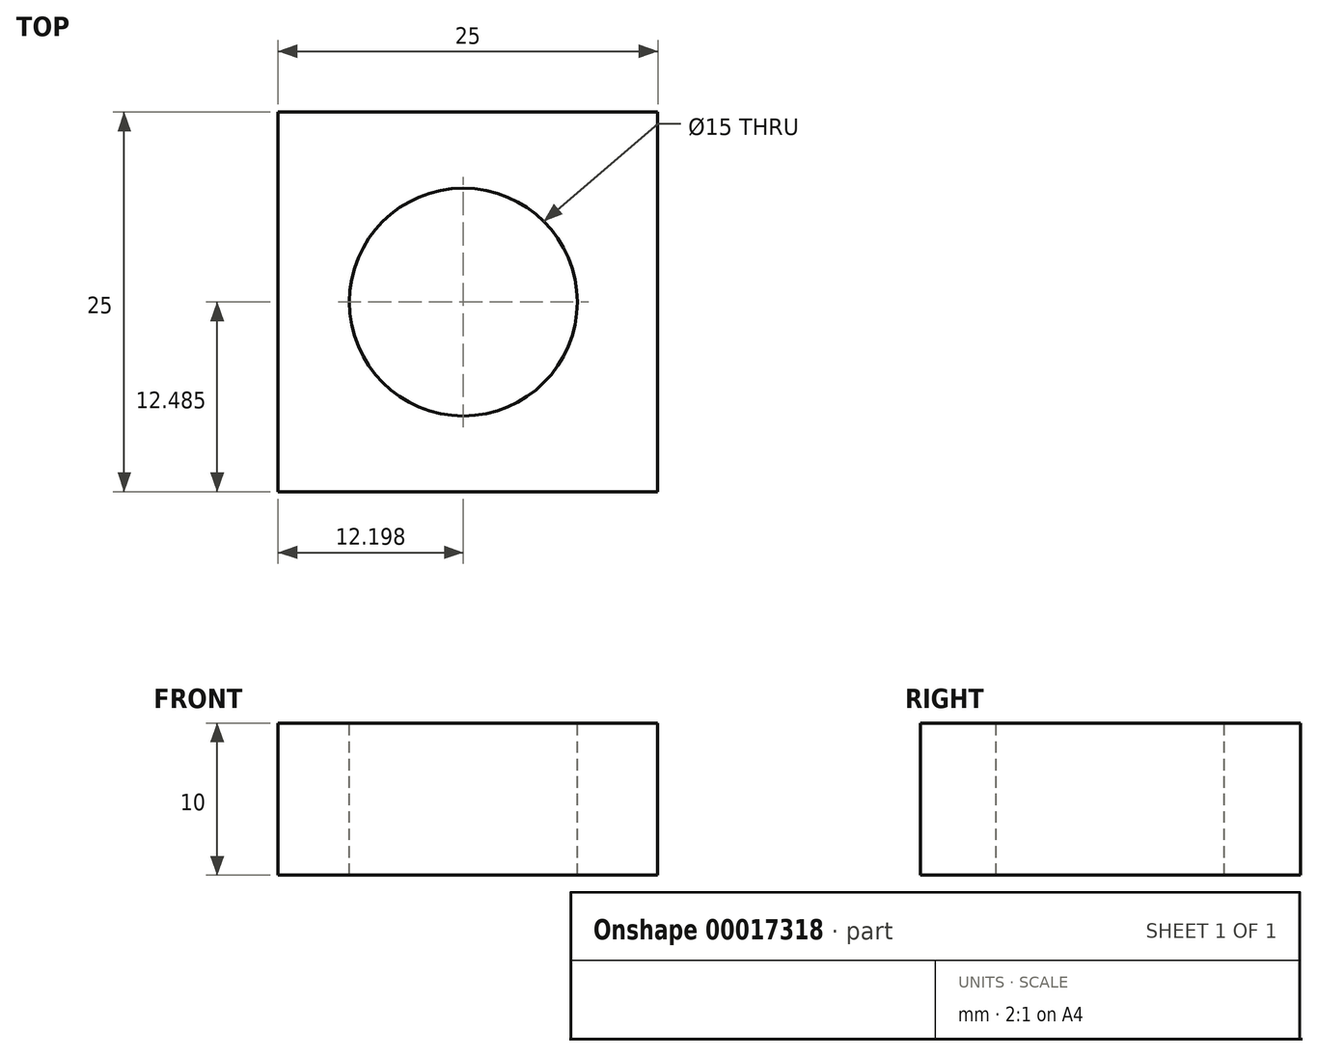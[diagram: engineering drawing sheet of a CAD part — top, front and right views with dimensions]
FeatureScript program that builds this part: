
annotation { "Feature Type Name" : "Feature", "Feature Type Description" : "" }
export const myFeature = defineFeature(function(context is Context, id is Id, definition is map)
    precondition{}
    {
        {
            var Q0;
            Q0=qCreatedBy(makeId("Front.planeOp"),FACE);
            var sketch = newSketch(context, id + "F0", { "sketchPlane" : qUnion([Q0])});
            skLineSegment(sketch, "E0", {"start": v(-4.12, 15.62) * mm, "end": v(-4.12, 5.62) * mm});
            skLineSegment(sketch, "E1", {"start": v(-4.12, 15.62) * mm, "end": v(20.88, 15.62) * mm});
            skLineSegment(sketch, "E2", {"start": v(20.88, 15.62) * mm, "end": v(20.88, 5.62) * mm});
            skLineSegment(sketch, "E3", {"start": v(-4.12, 5.62) * mm, "end": v(20.88, 5.62) * mm});
            skSolve(sketch);
        }
        {
            var Q0;
            Q0 = qSketchRegion(id + "F0", true);
            extrude(context, id + "F1", {"entities" : qUnion([Q0]), "depth" : 25 * mm});
        }
        {
            var Q0;
            Q0=makeQuery(id+"F1.opExtrude","SWEPT_FACE",FACE,{"disambiguationData":[OSD([sQuery(id+"F0.wireOp",EDGE,"E1")])]});
            var sketch = newSketch(context, id + "F2", { "sketchPlane" : qUnion([Q0])});
            skCircle(sketch, "E4", {"center": v(8.08, -12.52) * mm, "radius": 7.5 * mm});
            skSolve(sketch);
        }
        {
            var Q0;
            Q0=makeQuery(id+"F2.imprint","IMPRINT",FACE,{"disambiguationData":[TD([[makeQuery(id+"F2.imprint","IMPRINT",EDGE,{"derivedFrom":sQuery(id+"F2.wireOp",EDGE,"E4")}),1.0]])]});
            extrude(context, id + "F3", {"entities" : qUnion([Q0]), "operationType" : NewBodyOperationType.REMOVE, "endBound" : BoundingType.THROUGH_ALL, "oppositeDirection" : true, "depth" : 25 * mm});
        }
    });
